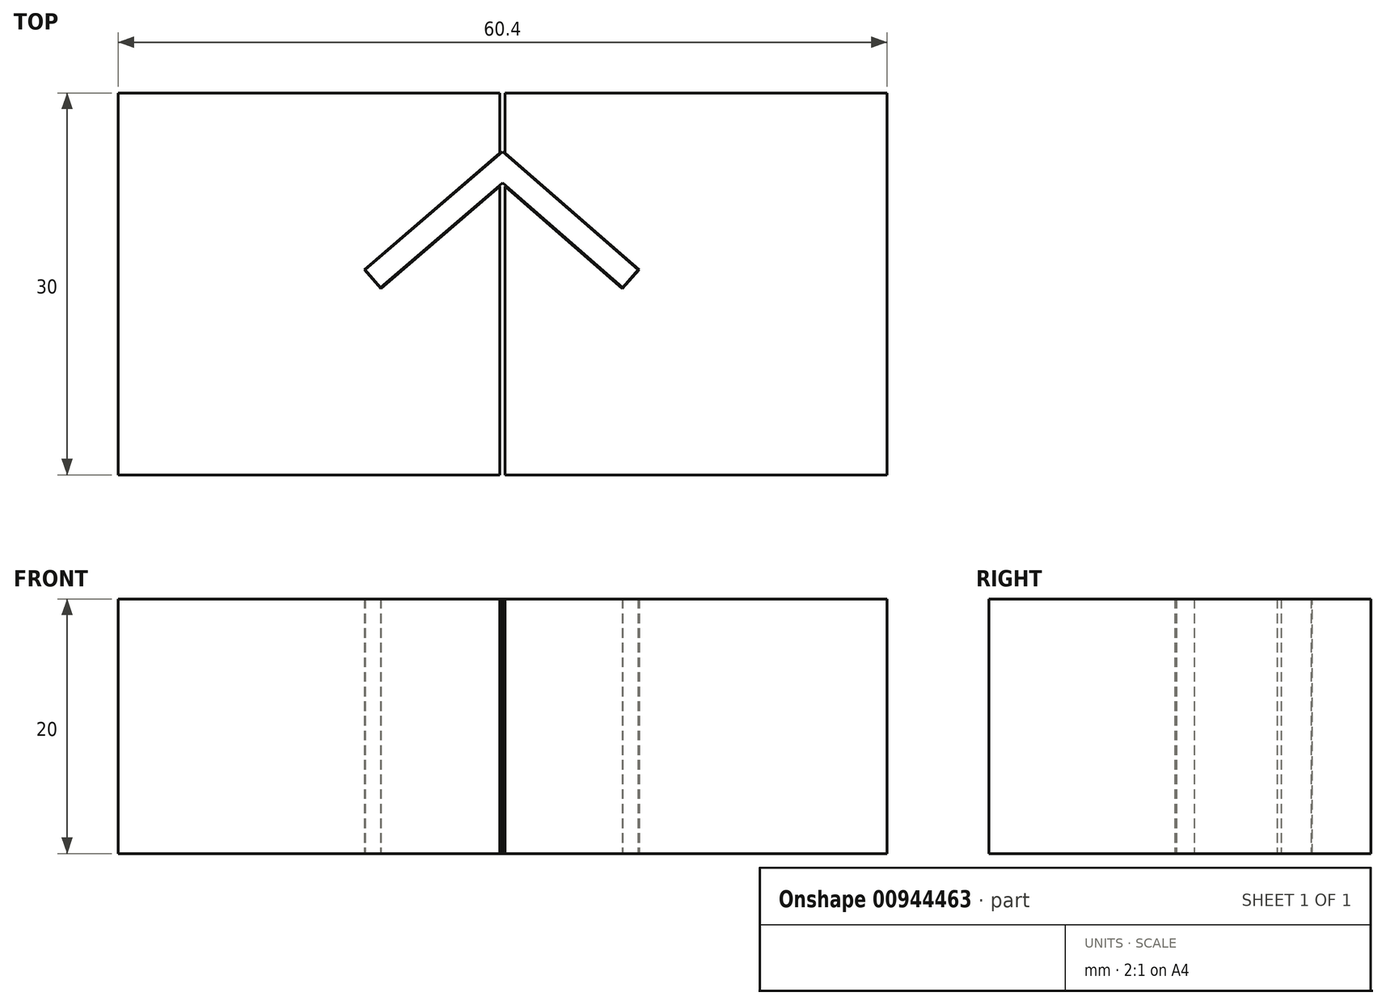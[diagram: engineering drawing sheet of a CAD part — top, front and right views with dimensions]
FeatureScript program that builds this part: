
annotation { "Feature Type Name" : "Feature", "Feature Type Description" : "" }
export const myFeature = defineFeature(function(context is Context, id is Id, definition is map)
    precondition{}
    {
        {
            var Q0;
            Q0=qCreatedBy(makeId("Top.planeOp"),FACE);
            var sketch = newSketch(context, id + "F0", { "sketchPlane" : qUnion([Q0])});
            skLineSegment(sketch, "E0.bottom", {"start": v(-30.2, 19.97) * mm, "end": v(-0.2, 19.97) * mm});
            skLineSegment(sketch, "E0.top", {"start": v(-30.2, -10.03) * mm, "end": v(-0.2, -10.03) * mm});
            skLineSegment(sketch, "E0.left", {"start": v(-30.2, 19.97) * mm, "end": v(-30.2, -10.03) * mm});
            skLineSegment(sketch, "E0.right", {"start": v(-0.2, 19.97) * mm, "end": v(-0.2, -10.03) * mm});
            skLineSegment(sketch, "E1.MirrorCS", {"start": v(30.2, 19.97) * mm, "end": v(0.2, 19.97) * mm});
            skLineSegment(sketch, "E2.MirrorCS", {"start": v(30.2, -10.03) * mm, "end": v(0.2, -10.03) * mm});
            skLineSegment(sketch, "E3.MirrorCS", {"start": v(0.2, 19.97) * mm, "end": v(0.2, -10.03) * mm});
            skLineSegment(sketch, "E4.MirrorCS", {"start": v(30.2, 19.97) * mm, "end": v(30.2, -10.03) * mm});
            skLineSegment(sketch, "E5", {"start": v(-10.84, 6.1) * mm, "end": v(0, 15.44) * mm});
            skLineSegment(sketch, "E6", {"start": v(0, 15.44) * mm, "end": v(10.73, 6.1) * mm});
            skLineSegment(sketch, "E7.0", {"start": v(-9.54, 4.58) * mm, "end": v(0, 12.8) * mm});
            skLineSegment(sketch, "E8.0", {"start": v(0, 12.8) * mm, "end": v(9.41, 4.59) * mm});
            skLineSegment(sketch, "E9", {"start": v(-9.54, 4.58) * mm, "end": v(-10.84, 6.1) * mm});
            skLineSegment(sketch, "E10", {"start": v(9.41, 4.59) * mm, "end": v(10.73, 6.1) * mm});
            skSolve(sketch);
        }
        {
            var Q0;
            {var subQ1=sQuery(id+"F0.wireOp",EDGE,"E0.bottom");Q0=makeQuery(id+"F0.imprint","IMPRINT",FACE,{"disambiguationData":[TD([[makeQuery(id+"F0.imprint","IMPRINT",EDGE,{"derivedFrom":subQ1}),-1.0]])]});}
            var Q1;
            {var subQ5=sQuery(id+"F0.wireOp",EDGE,"E1.MirrorCS");Q1=makeQuery(id+"F0.imprint","IMPRINT",FACE,{"disambiguationData":[TD([[makeQuery(id+"F0.imprint","IMPRINT",EDGE,{"derivedFrom":subQ5}),1.0]])]});}
            extrude(context, id + "F1", {"entities" : qUnion([Q0, Q1]), "depth" : 20 * mm, "offsetDistance" : 25 * mm});
        }
        {
            var Q0;
            Q0=qCreatedBy(makeId("Top.planeOp"),FACE);
            var sketch = newSketch(context, id + "F2", { "sketchPlane" : qUnion([Q0])});
            skLineSegment(sketch, "E11.0", {"start": v(-10.84, 6.1) * mm, "end": v(-0.2, 15.27) * mm, "construction": true});
            skPoint(sketch, "E12.0", {"position": v(-10.2, 5.34) * mm});
            skLineSegment(sketch, "E13.0", {"start": v(-9.54, 4.58) * mm, "end": v(-10.84, 6.1) * mm, "construction": true});
            skLineSegment(sketch, "E14.0", {"start": v(-9.54, 4.58) * mm, "end": v(-0.2, 12.63) * mm, "construction": true});
            skLineSegment(sketch, "E15.0", {"start": v(0.2, 12.61) * mm, "end": v(9.41, 4.59) * mm, "construction": true});
            skPoint(sketch, "E16.0", {"position": v(10.73, 6.1) * mm});
            skLineSegment(sketch, "E17.0", {"start": v(9.41, 4.59) * mm, "end": v(10.73, 6.1) * mm, "construction": true});
            skLineSegment(sketch, "E18.0", {"start": v(0.2, 15.26) * mm, "end": v(10.73, 6.1) * mm, "construction": true});
            skLineSegment(sketch, "E19.0", {"start": v(-9.5, 4.62) * mm, "end": v(-10.8, 6.13) * mm});
            skLineSegment(sketch, "E20.0", {"start": v(9.38, 4.62) * mm, "end": v(10.7, 6.13) * mm});
            skLineSegment(sketch, "E21.0", {"start": v(0, 12.92) * mm, "end": v(9.48, 4.66) * mm});
            skLineSegment(sketch, "E22.0", {"start": v(0, 15.37) * mm, "end": v(10.7, 6.06) * mm});
            skLineSegment(sketch, "E23.0", {"start": v(-9.6, 4.66) * mm, "end": v(0, 12.92) * mm});
            skLineSegment(sketch, "E24.0", {"start": v(-10.81, 6.06) * mm, "end": v(0, 15.37) * mm});
            skSolve(sketch);
        }
        {
            var Q0;
            Q0 = qSketchRegion(id + "F2", true);
            extrude(context, id + "F3", {"entities" : qUnion([Q0]), "depth" : 20 * mm, "offsetDistance" : 25 * mm});
        }
    });
